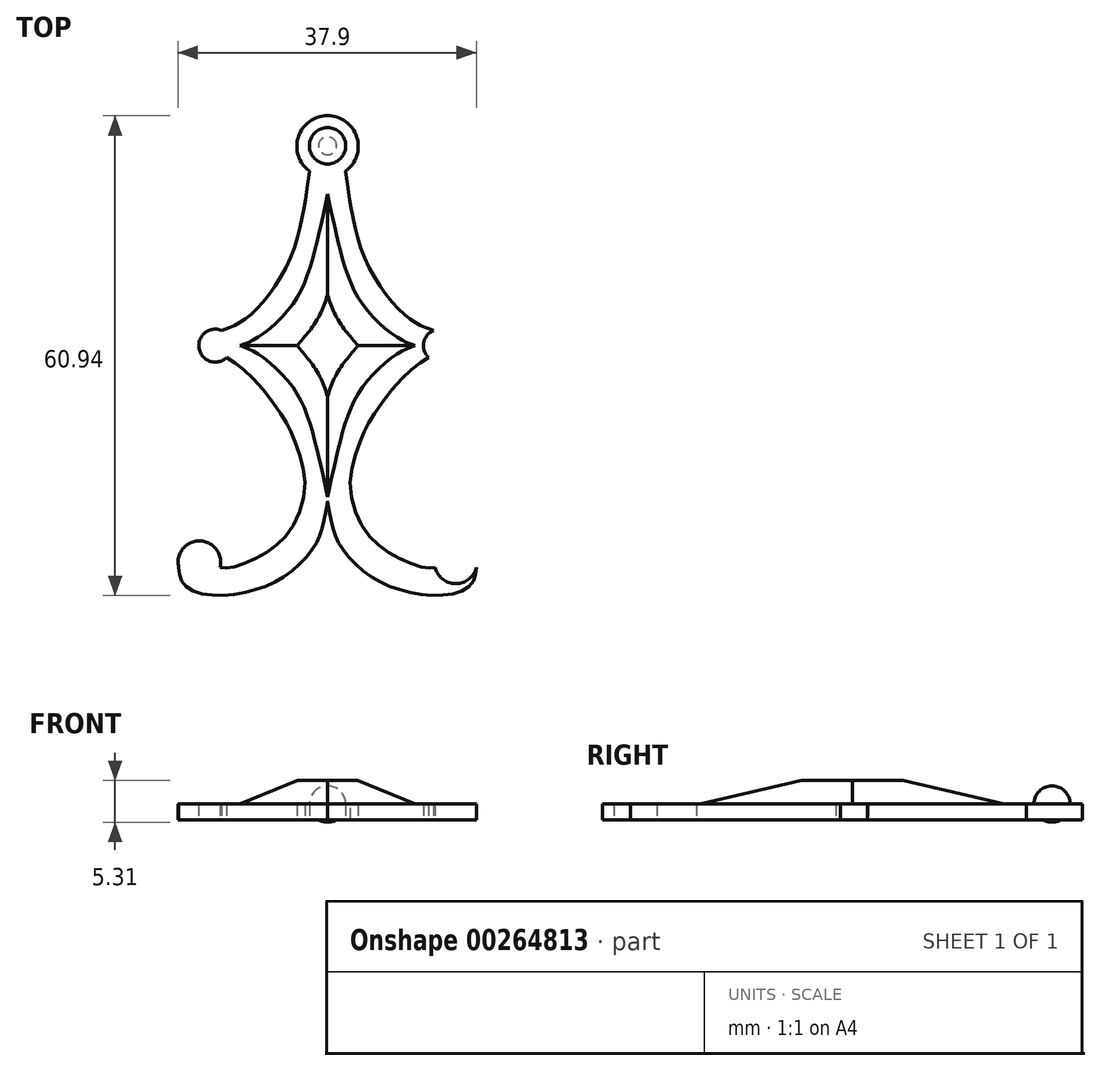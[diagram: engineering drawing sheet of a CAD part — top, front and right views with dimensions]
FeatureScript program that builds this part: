
annotation { "Feature Type Name" : "Feature", "Feature Type Description" : "" }
export const myFeature = defineFeature(function(context is Context, id is Id, definition is map)
    precondition{}
    {
        {
            var Q0;
            Q0=qCreatedBy(makeId("Top.planeOp"),FACE);
            var sketch = newSketch(context, id + "F0", { "sketchPlane" : qUnion([Q0])});
            skLineSegment(sketch, "E0", {"start": v(0, 33.8) * mm, "end": v(0, -37.22) * mm, "construction": true});
            skCircle(sketch, "E1", {"center": v(0, 25.31) * mm, "radius": 3.9 * mm});
            skCircle(sketch, "E2", {"center": v(-14.27, 0) * mm, "radius": 2.1 * mm});
            skCircle(sketch, "E3", {"center": v(-16.28, -27.52) * mm, "radius": 2.7 * mm});
            skFitSpline(sketch, "E4", {"points": [v(-2.28, 22.15) * mm, v(-2.86, 18.19) * mm, v(-4.87, 10.8) * mm, v(-9.24, 4.43) * mm, v(-12, 2.48) * mm, v(-13.47, 1.93) * mm], "startDerivative": vector(-2.47, -19.26) * mm, "endDerivative": vector(-10.02, -4.61) * mm});
            skFitSpline(sketch, "E5", {"points": [v(-12.83, -1.52) * mm, v(-9.86, -3.77) * mm, v(-5.8, -8.89) * mm, v(-4.23, -11.97) * mm, v(-2.88, -17.67) * mm, v(-4.97, -23.76) * mm, v(-8.7, -26.8) * mm, v(-12.36, -28.22) * mm, v(-13.65, -28.15) * mm], "startDerivative": vector(24.45, -15.51) * mm, "endDerivative": vector(-16.48, 3.15) * mm});
            skFitSpline(sketch, "E6", {"points": [v(-18.91, -28.15) * mm, v(-18.28, -30.3) * mm, v(-15.12, -31.66) * mm, v(-9.7, -31.15) * mm, v(-5.25, -29.18) * mm, v(-2.03, -26.02) * mm, v(-0.8, -23.53) * mm, v(0, -19.75) * mm], "startDerivative": vector(2.05, -21.3) * mm, "endDerivative": vector(4.78, 28.06) * mm});
            skFitSpline(sketch, "E7.MirrorCS", {"points": [v(2.28, 22.15) * mm, v(2.86, 18.19) * mm, v(4.87, 10.8) * mm, v(9.24, 4.43) * mm, v(12, 2.48) * mm, v(13.47, 1.93) * mm], "startDerivative": vector(2.47, -19.26) * mm, "endDerivative": vector(10.02, -4.61) * mm});
            skCircle(sketch, "E8.MirrorC", {"center": v(14.27, 0) * mm, "radius": 2.1 * mm});
            skFitSpline(sketch, "E9.MirrorCS", {"points": [v(12.83, -1.52) * mm, v(9.86, -3.77) * mm, v(5.8, -8.89) * mm, v(4.23, -11.97) * mm, v(2.88, -17.67) * mm, v(4.97, -23.76) * mm, v(8.7, -26.8) * mm, v(12.36, -28.22) * mm, v(13.65, -28.15) * mm], "startDerivative": vector(-24.45, -15.51) * mm, "endDerivative": vector(16.48, 3.15) * mm});
            skCircle(sketch, "E10.MirrorC", {"center": v(16.28, -27.52) * mm, "radius": 2.7 * mm});
            skFitSpline(sketch, "E11.MirrorCS", {"points": [v(18.91, -28.15) * mm, v(18.28, -30.3) * mm, v(15.12, -31.66) * mm, v(9.7, -31.15) * mm, v(5.25, -29.18) * mm, v(2.03, -26.02) * mm, v(0.8, -23.53) * mm, v(0, -19.75) * mm], "startDerivative": vector(-2.05, -21.3) * mm, "endDerivative": vector(-4.78, 28.06) * mm});
            skSolve(sketch);
        }
        {
            var Q0;
            {var subQ7=sQuery(id+"F0.wireOp",EDGE,"E4");Q0=makeQuery(id+"F0.imprint","IMPRINT",FACE,{"disambiguationData":[TD([[makeQuery(id+"F0.imprint","IMPRINT",EDGE,{"derivedFrom":subQ7}),1.0]])]});}
            var Q1;
            {var subQ0=sQuery(id+"F0.wireOp",EDGE,"E1");var subQ1=makeQuery(id+"F0.imprint","INTERSECT",VERTEX,{"derivedFrom":[subQ0,sQuery(id+"F0.wireOp",EDGE,"E4")]});Q1=makeQuery(id+"F0.imprint","IMPRINT",FACE,{"disambiguationData":[TD([[makeQuery(id+"F0.imprint","IMPRINT",EDGE,{"disambiguationData":[TD([[subQ1,-1.0]])],"derivedFrom":subQ0}),1.0]])]});}
            var Q2;
            {var subQ0=sQuery(id+"F0.wireOp",EDGE,"E2");var subQ1=makeQuery(id+"F0.imprint","INTERSECT",VERTEX,{"derivedFrom":[subQ0,sQuery(id+"F0.wireOp",EDGE,"E4")]});Q2=makeQuery(id+"F0.imprint","IMPRINT",FACE,{"disambiguationData":[TD([[makeQuery(id+"F0.imprint","IMPRINT",EDGE,{"disambiguationData":[TD([[subQ1,-1.0]])],"derivedFrom":subQ0}),1.0]])]});}
            var Q3;
            {var subQ0=sQuery(id+"F0.wireOp",EDGE,"E8.MirrorC");var subQ1=makeQuery(id+"F0.imprint","INTERSECT",VERTEX,{"derivedFrom":[sQuery(id+"F0.wireOp",EDGE,"E7.MirrorCS"),subQ0]});Q3=makeQuery(id+"F0.imprint","IMPRINT",FACE,{"disambiguationData":[TD([[makeQuery(id+"F0.imprint","IMPRINT",EDGE,{"disambiguationData":[TD([[subQ1,-1.0]])],"derivedFrom":subQ0}),-1.0]])]});}
            var Q4;
            {var subQ0=sQuery(id+"F0.wireOp",EDGE,"E10.MirrorC");var subQ1=makeQuery(id+"F0.imprint","INTERSECT",VERTEX,{"derivedFrom":[sQuery(id+"F0.wireOp",EDGE,"E9.MirrorCS"),subQ0]});Q4=makeQuery(id+"F0.imprint","IMPRINT",FACE,{"disambiguationData":[TD([[makeQuery(id+"F0.imprint","IMPRINT",EDGE,{"disambiguationData":[TD([[subQ1,1.0]])],"derivedFrom":subQ0}),-1.0]])]});}
            var Q5;
            {var subQ0=sQuery(id+"F0.wireOp",EDGE,"E3");var subQ1=makeQuery(id+"F0.imprint","INTERSECT",VERTEX,{"derivedFrom":[subQ0,sQuery(id+"F0.wireOp",EDGE,"E5")]});Q5=makeQuery(id+"F0.imprint","IMPRINT",FACE,{"disambiguationData":[TD([[makeQuery(id+"F0.imprint","IMPRINT",EDGE,{"disambiguationData":[TD([[subQ1,1.0]])],"derivedFrom":subQ0}),1.0]])]});}
            extrude(context, id + "F1", {"entities" : qUnion([Q0, Q1, Q2, Q3, Q4, Q5]), "depth" : 2 * mm, "offsetDistance" : 25 * mm});
        }
        {
            var Q0;
            Q0=makeQuery(id+"F1.opExtrude","CAP_FACE",FACE,{"disambiguationData":[OSD([sQuery(id+"F0.wireOp",EDGE,"E1"),sQuery(id+"F0.wireOp",EDGE,"E2"),sQuery(id+"F0.wireOp",EDGE,"E3"),sQuery(id+"F0.wireOp",EDGE,"E4"),sQuery(id+"F0.wireOp",EDGE,"E5"),sQuery(id+"F0.wireOp",EDGE,"E6"),sQuery(id+"F0.wireOp",EDGE,"E7.MirrorCS"),sQuery(id+"F0.wireOp",EDGE,"E8.MirrorC"),sQuery(id+"F0.wireOp",EDGE,"E9.MirrorCS"),sQuery(id+"F0.wireOp",EDGE,"E10.MirrorC"),sQuery(id+"F0.wireOp",EDGE,"E11.MirrorCS")])],"isStart":false});
            var sketch = newSketch(context, id + "F2", { "sketchPlane" : qUnion([Q0])});
            skFitSpline(sketch, "E12", {"points": [v(0, 19.25) * mm, v(-2, 10.7) * mm, v(-4.6, 5.01) * mm, v(-9, 0.98) * mm, v(-11.13, 0) * mm], "startDerivative": vector(-6.02, -28.64) * mm, "endDerivative": vector(-12, -4.3) * mm});
            skFitSpline(sketch, "E13.MirrorCS", {"points": [v(0, 19.25) * mm, v(2, 10.7) * mm, v(4.6, 5.01) * mm, v(9, 0.98) * mm, v(11.13, 0) * mm], "startDerivative": vector(6.02, -28.64) * mm, "endDerivative": vector(12, -4.3) * mm});
            skFitSpline(sketch, "E14.MirrorCS", {"points": [v(0, -19.25) * mm, v(-2, -10.7) * mm, v(-4.6, -5.01) * mm, v(-9, -0.98) * mm, v(-11.13, 0) * mm], "startDerivative": vector(-6.02, 28.64) * mm, "endDerivative": vector(-12, 4.3) * mm});
            skFitSpline(sketch, "E15.MirrorCS", {"points": [v(0, -19.25) * mm, v(2, -10.7) * mm, v(4.6, -5.01) * mm, v(9, -0.98) * mm, v(11.13, 0) * mm], "startDerivative": vector(6.02, 28.64) * mm, "endDerivative": vector(12, 4.3) * mm});
            skSolve(sketch);
        }
        {
            var Q0;
            Q0=makeQuery(id+"F1.opExtrude","CAP_FACE",FACE,{"disambiguationData":[OSD([sQuery(id+"F0.wireOp",EDGE,"E1"),sQuery(id+"F0.wireOp",EDGE,"E2"),sQuery(id+"F0.wireOp",EDGE,"E3"),sQuery(id+"F0.wireOp",EDGE,"E4"),sQuery(id+"F0.wireOp",EDGE,"E5"),sQuery(id+"F0.wireOp",EDGE,"E6"),sQuery(id+"F0.wireOp",EDGE,"E7.MirrorCS"),sQuery(id+"F0.wireOp",EDGE,"E8.MirrorC"),sQuery(id+"F0.wireOp",EDGE,"E9.MirrorCS"),sQuery(id+"F0.wireOp",EDGE,"E10.MirrorC"),sQuery(id+"F0.wireOp",EDGE,"E11.MirrorCS")])],"isStart":false});
            cPlane(context, id + "F3", {"entities" : qUnion([Q0]), "cplaneType" : CPlaneType.OFFSET, "offset" : 3 * mm, "width" : 150 * mm, "height" : 150 * mm});
        }
        {
            var Q0;
            Q0=qCreatedBy(id+"F3.planeOp",FACE);
            var sketch = newSketch(context, id + "F4", { "sketchPlane" : qUnion([Q0])});
            skFitSpline(sketch, "E16", {"points": [v(0, 6.45) * mm, v(-1, 3.89) * mm, v(-2.51, 1.61) * mm, v(-3.84, 0) * mm], "startDerivative": vector(-2.45, -7.48) * mm, "endDerivative": vector(-4.28, -5.04) * mm});
            skFitSpline(sketch, "E17.MirrorCS", {"points": [v(0, 6.45) * mm, v(1, 3.89) * mm, v(2.51, 1.61) * mm, v(3.84, 0) * mm], "startDerivative": vector(2.45, -7.48) * mm, "endDerivative": vector(4.28, -5.04) * mm});
            skFitSpline(sketch, "E18.MirrorCS", {"points": [v(0, -6.45) * mm, v(-1, -3.89) * mm, v(-2.51, -1.61) * mm, v(-3.84, 0) * mm], "startDerivative": vector(-2.45, 7.48) * mm, "endDerivative": vector(-4.28, 5.04) * mm});
            skFitSpline(sketch, "E19.MirrorCS", {"points": [v(0, -6.45) * mm, v(1, -3.89) * mm, v(2.51, -1.61) * mm, v(3.84, 0) * mm], "startDerivative": vector(2.45, 7.48) * mm, "endDerivative": vector(4.28, 5.04) * mm});
            skSolve(sketch);
        }
        {
            var Q1;
            Q1=makeQuery(id+"F2.imprint","IMPRINT",FACE,{"disambiguationData":[TD([[makeQuery(id+"F2.imprint","IMPRINT",EDGE,{"derivedFrom":sQuery(id+"F2.wireOp",EDGE,"E12")}),1.0]])]});
            var Q2;
            Q2=makeQuery(id+"F4.imprint","IMPRINT",FACE,{"disambiguationData":[TD([[makeQuery(id+"F4.imprint","IMPRINT",EDGE,{"derivedFrom":sQuery(id+"F4.wireOp",EDGE,"E16")}),1.0]])]});
            loft(context, id + "F5", {"operationType" : NewBodyOperationType.ADD, "sheetProfilesArray" : [{ "sheetProfileEntities" : qUnion([Q1]) }, { "sheetProfileEntities" : qUnion([Q2]) }]});
        }
        {
            var Q0;
            Q0=makeQuery(id+"F1.opExtrude","CAP_FACE",FACE,{"disambiguationData":[OSD([sQuery(id+"F0.wireOp",EDGE,"E1"),sQuery(id+"F0.wireOp",EDGE,"E2"),sQuery(id+"F0.wireOp",EDGE,"E3"),sQuery(id+"F0.wireOp",EDGE,"E4"),sQuery(id+"F0.wireOp",EDGE,"E5"),sQuery(id+"F0.wireOp",EDGE,"E6"),sQuery(id+"F0.wireOp",EDGE,"E7.MirrorCS"),sQuery(id+"F0.wireOp",EDGE,"E8.MirrorC"),sQuery(id+"F0.wireOp",EDGE,"E9.MirrorCS"),sQuery(id+"F0.wireOp",EDGE,"E10.MirrorC"),sQuery(id+"F0.wireOp",EDGE,"E11.MirrorCS")])],"isStart":false});
            var sketch = newSketch(context, id + "F6", { "sketchPlane" : qUnion([Q0])});
            skCircle(sketch, "E20", {"center": v(0, 25.39) * mm, "radius": 2.3 * mm});
            skLineSegment(sketch, "E21", {"start": v(0, 27.7) * mm, "end": v(0, 23.08) * mm});
            skSolve(sketch);
        }
        {
            var Q0;
            {var subQ0=sQuery(id+"F6.wireOp",EDGE,"E21");Q0=makeQuery(id+"F6.imprint","IMPRINT",FACE,{"disambiguationData":[TD([[makeQuery(id+"F6.imprint","IMPRINT",EDGE,{"derivedFrom":subQ0}),-1.0]])]});}
            var Q1;
            Q1=sQuery(id+"F6.wireOp",EDGE,"E21");
            revolve(context, id + "F7", {"operationType" : NewBodyOperationType.ADD, "entities" : qUnion([Q0]), "axis" : qUnion([Q1]), "revolveType" : RevolveType.FULL});
        }
    });
